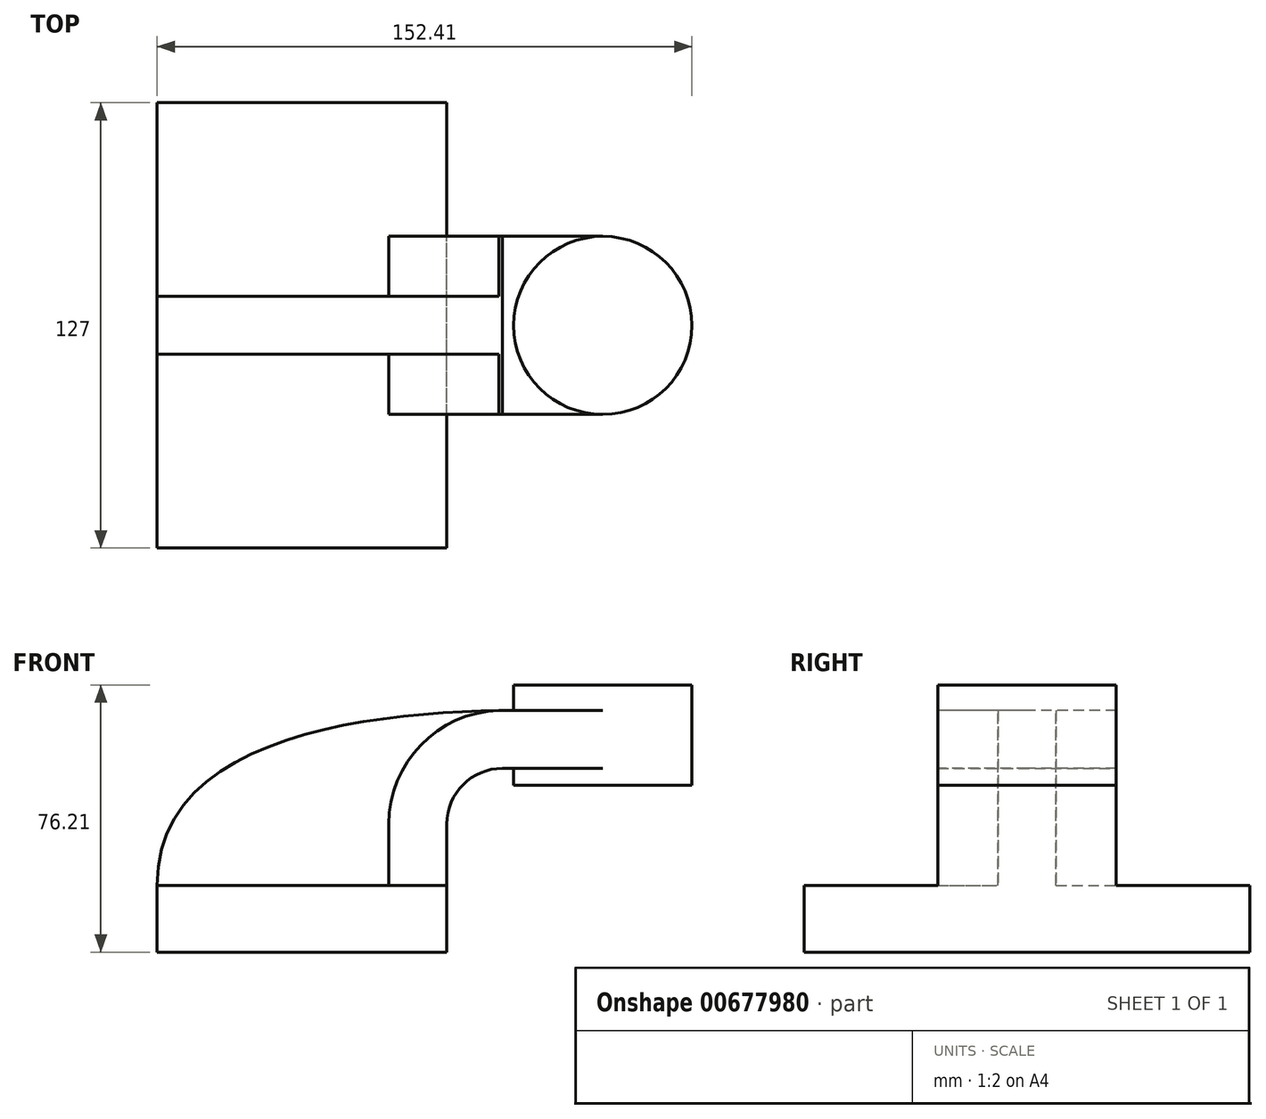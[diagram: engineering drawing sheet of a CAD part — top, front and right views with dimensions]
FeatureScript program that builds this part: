
annotation { "Feature Type Name" : "Feature", "Feature Type Description" : "" }
export const myFeature = defineFeature(function(context is Context, id is Id, definition is map)
    precondition{}
    {
        {
            var Q0;
            Q0=qCreatedBy(makeId("Front.planeOp"),FACE);
            var sketch = newSketch(context, id + "F0", { "sketchPlane" : qUnion([Q0])});
            skLineSegment(sketch, "E0.bottom", {"start": v(-41.28, 9.52) * mm, "end": v(41.28, 9.53) * mm});
            skLineSegment(sketch, "E0.top", {"start": v(-41.28, -9.52) * mm, "end": v(41.28, -9.52) * mm});
            skLineSegment(sketch, "E0.left", {"start": v(-41.28, 9.52) * mm, "end": v(-41.28, -9.53) * mm});
            skLineSegment(sketch, "E0.right", {"start": v(41.27, 9.53) * mm, "end": v(41.28, -9.52) * mm});
            skPoint(sketch, "E0.middle", {"position": v(0, 0) * mm});
            skLineSegment(sketch, "E1.bottom", {"start": v(60.33, 66.67) * mm, "end": v(111.13, 66.67) * mm});
            skLineSegment(sketch, "E1.top", {"start": v(60.33, 38.1) * mm, "end": v(111.13, 38.1) * mm});
            skLineSegment(sketch, "E1.left", {"start": v(60.33, 66.68) * mm, "end": v(60.33, 38.1) * mm});
            skLineSegment(sketch, "E1.right", {"start": v(111.13, 66.68) * mm, "end": v(111.13, 38.1) * mm});
            skPoint(sketch, "E1.middle", {"position": v(85.73, 52.39) * mm});
            skLineSegment(sketch, "E2", {"start": v(41.27, 9.53) * mm, "end": v(41.27, 27) * mm});
            skArc(sketch, "E3", {"start": v(41.27, 27) * mm, "mid": v(45.92, 38.23) * mm, "end": v(57.15, 42.88) * mm});
            skLineSegment(sketch, "E4", {"start": v(57.15, 42.88) * mm, "end": v(86, 42.88) * mm});
            skLineSegment(sketch, "E5.0", {"start": v(57.15, 59.39) * mm, "end": v(86, 59.39) * mm});
            skArc(sketch, "E5.1", {"start": v(24.77, 27) * mm, "mid": v(34.25, 49.9) * mm, "end": v(57.15, 59.39) * mm});
            skLineSegment(sketch, "E5.2", {"start": v(24.77, 27) * mm, "end": v(24.77, 39.74) * mm});
            skLineSegment(sketch, "E6", {"start": v(85.73, 38.1) * mm, "end": v(85.73, 66.68) * mm});
            skLineSegment(sketch, "E7", {"start": v(24.77, 27) * mm, "end": v(24.77, 9.53) * mm});
            skFitSpline(sketch, "E8", {"points": [v(-41.28, 9.52) * mm, v(57.15, 59.39) * mm], "startDerivative": vector(-0.59, 127.48) * mm, "endDerivative": vector(115.31, 1.7) * mm});
            skSolve(sketch);
        }
        {
            var Q0;
            Q0=makeQuery(id+"F0.imprint","IMPRINT",FACE,{"disambiguationData":[TD([[makeQuery(id+"F0.imprint","IMPRINT",EDGE,{"derivedFrom":sQuery(id+"F0.wireOp",EDGE,"E0.top")}),1.0]])]});
            extrude(context, id + "F1", {"entities" : qUnion([Q0]), "endBound" : BoundingType.SYMMETRIC, "depth" : 127 * mm, "offsetDistance" : 25.4 * mm});
        }
        {
            var Q0;
            {var subQ1=sQuery(id+"F0.wireOp",EDGE,"E2");Q0=makeQuery(id+"F0.imprint","IMPRINT",FACE,{"disambiguationData":[TD([[makeQuery(id+"F0.imprint","IMPRINT",EDGE,{"derivedFrom":subQ1}),1.0]])]});}
            var Q1;
            {var subQ0=sQuery(id+"F0.wireOp",EDGE,"E5.0");var subQ1=sQuery(id+"F0.wireOp",EDGE,"E1.left");var subQ2=makeQuery(id+"F0.imprint","INTERSECT",VERTEX,{"derivedFrom":[subQ1,subQ0]});Q1=makeQuery(id+"F0.imprint","IMPRINT",FACE,{"disambiguationData":[TD([[makeQuery(id+"F0.imprint","IMPRINT",EDGE,{"disambiguationData":[TD([[subQ2,-1.0]])],"derivedFrom":subQ1}),1.0]])]});}
            extrude(context, id + "F2", {"entities" : qUnion([Q0, Q1]), "operationType" : NewBodyOperationType.ADD, "endBound" : BoundingType.SYMMETRIC, "depth" : 50.8 * mm, "offsetDistance" : 25.4 * mm});
        }
        {
            var Q0;
            {var subQ3=sQuery(id+"F0.wireOp",EDGE,"E7");Q0=makeQuery(id+"F0.imprint","IMPRINT",FACE,{"disambiguationData":[TD([[makeQuery(id+"F0.imprint","IMPRINT",EDGE,{"derivedFrom":subQ3}),-1.0]])]});}
            extrude(context, id + "F3", {"entities" : qUnion([Q0]), "operationType" : NewBodyOperationType.ADD, "endBound" : BoundingType.SYMMETRIC, "depth" : 16.5 * mm, "offsetDistance" : 25.4 * mm});
        }
        {
            var Q0;
            {var subQ0=sQuery(id+"F0.wireOp",EDGE,"E1.right");Q0=makeQuery(id+"F0.imprint","IMPRINT",FACE,{"disambiguationData":[TD([[makeQuery(id+"F0.imprint","IMPRINT",EDGE,{"derivedFrom":subQ0}),-1.0]])]});}
            var Q1;
            Q1=sQuery(id+"F0.wireOp",EDGE,"E6");
            revolve(context, id + "F4", {"operationType" : NewBodyOperationType.ADD, "entities" : qUnion([Q0]), "axis" : qUnion([Q1]), "revolveType" : RevolveType.FULL});
        }
    });
